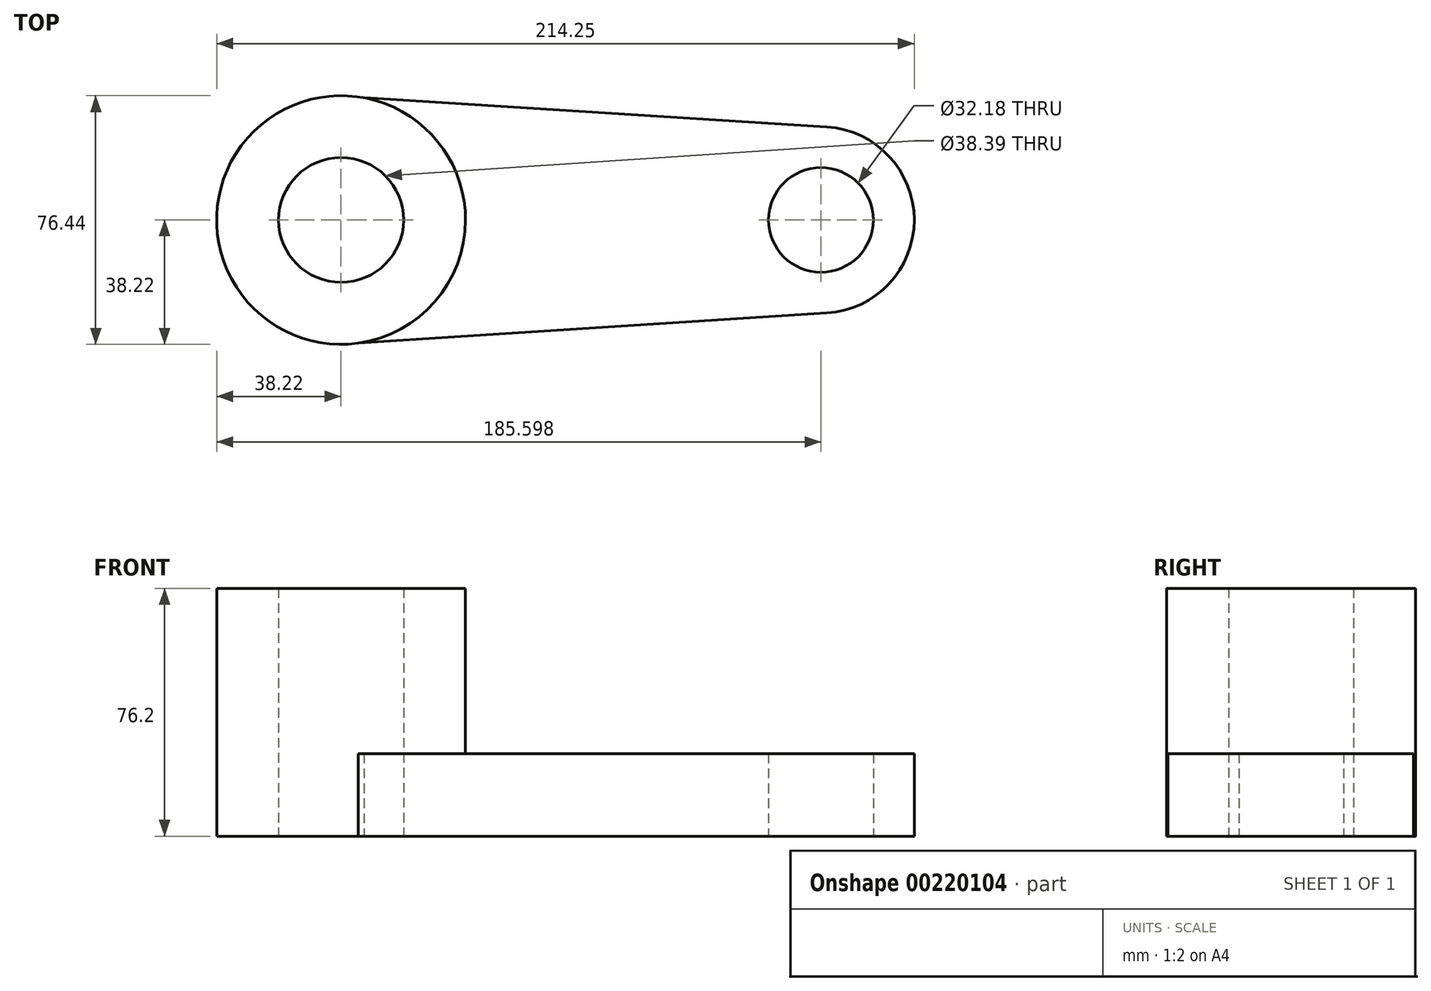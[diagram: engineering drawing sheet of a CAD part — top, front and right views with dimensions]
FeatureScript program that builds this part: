
annotation { "Feature Type Name" : "Feature", "Feature Type Description" : "" }
export const myFeature = defineFeature(function(context is Context, id is Id, definition is map)
    precondition{}
    {
        {
            var Q0;
            Q0=qCreatedBy(makeId("Top.planeOp"),FACE);
            var sketch = newSketch(context, id + "F0", { "sketchPlane" : qUnion([Q0])});
            skCircle(sketch, "E0", {"center": v(-72.35, 0) * mm, "radius": 38.22 * mm});
            skCircle(sketch, "E1", {"center": v(-72.35, 0) * mm, "radius": 19.2 * mm});
            skArc(sketch, "E2", {"start": v(76.87, -28.6) * mm, "mid": v(103.68, 0.02) * mm, "end": v(76.83, 28.6) * mm});
            skCircle(sketch, "E3", {"center": v(75.03, 0) * mm, "radius": 16.09 * mm});
            skLineSegment(sketch, "E4", {"start": v(-67.15, -37.86) * mm, "end": v(76.87, -28.6) * mm});
            skLineSegment(sketch, "E5", {"start": v(-65.35, 37.57) * mm, "end": v(76.83, 28.6) * mm});
            skSolve(sketch);
        }
        {
            var Q0;
            {var subQ1=sQuery(id+"F0.wireOp",EDGE,"E2");Q0=makeQuery(id+"F0.imprint","IMPRINT",FACE,{"disambiguationData":[TD([[makeQuery(id+"F0.imprint","IMPRINT",EDGE,{"derivedFrom":subQ1}),1.0]])]});}
            extrude(context, id + "F1", {"entities" : qUnion([Q0]), "depth" : 25.4 * mm});
        }
        {
            var Q0;
            Q0=makeQuery(id+"F0.imprint","IMPRINT",FACE,{"disambiguationData":[TD([[makeQuery(id+"F0.imprint","IMPRINT",EDGE,{"derivedFrom":sQuery(id+"F0.wireOp",EDGE,"E1")}),-1.0]])]});
            extrude(context, id + "F2", {"entities" : qUnion([Q0]), "operationType" : NewBodyOperationType.ADD, "depth" : 76.2 * mm});
        }
    });
